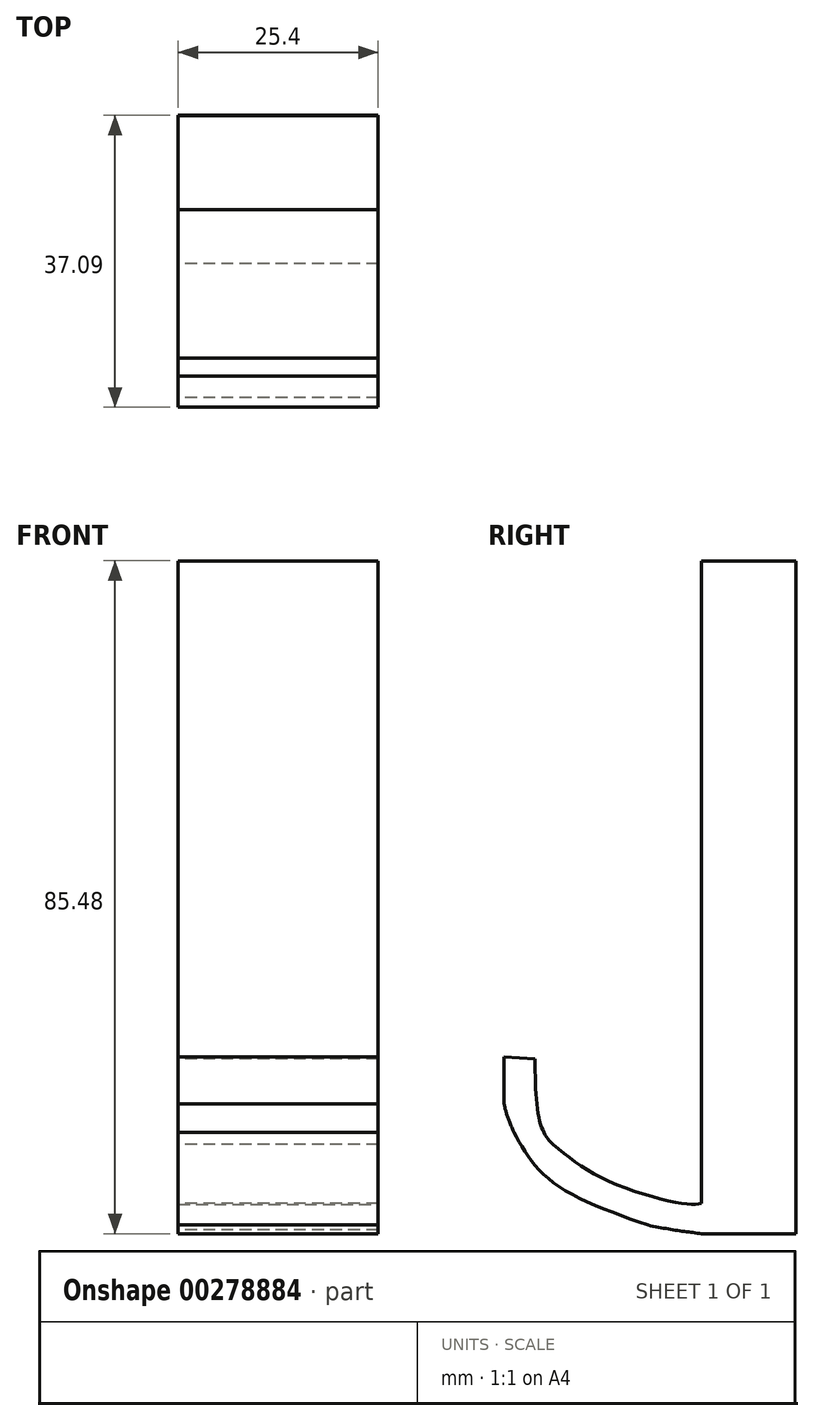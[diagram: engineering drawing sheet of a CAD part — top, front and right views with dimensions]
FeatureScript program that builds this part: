
annotation { "Feature Type Name" : "Feature", "Feature Type Description" : "" }
export const myFeature = defineFeature(function(context is Context, id is Id, definition is map)
    precondition{}
    {
        {
            var Q0;
            Q0=qCreatedBy(makeId("Right.planeOp"),FACE);
            var sketch = newSketch(context, id + "F0", { "sketchPlane" : qUnion([Q0])});
            skLineSegment(sketch, "E0", {"start": v(0, 56.23) * mm, "end": v(0, 0) * mm});
            skLineSegment(sketch, "E1", {"start": v(0, 0) * mm, "end": v(0, -25.43) * mm});
            skLineSegment(sketch, "E2", {"start": v(0, 56.23) * mm, "end": v(11.98, 56.23) * mm});
            skLineSegment(sketch, "E3", {"start": v(11.98, 56.23) * mm, "end": v(11.98, -28.76) * mm});
            skLineSegment(sketch, "E4", {"start": v(0, -29.25) * mm, "end": v(12, -29.25) * mm});
            skLineSegment(sketch, "E5", {"start": v(12, -29.25) * mm, "end": v(11.98, -28.76) * mm});
            skFitSpline(sketch, "E6", {"points": [v(-18.86, -17.93) * mm, v(-12.1, -22.45) * mm, v(-2.16, -25.45) * mm, v(0, -25.43) * mm], "startDerivative": vector(15.44, -12.93) * mm, "endDerivative": vector(8.77, 1.1) * mm});
            skLineSegment(sketch, "E7", {"start": v(-25.1, -10.73) * mm, "end": v(-25.1, -6.83) * mm});
            skLineSegment(sketch, "E8", {"start": v(-25.1, -6.83) * mm, "end": v(-21.14, -7.06) * mm});
            skFitSpline(sketch, "E9", {"points": [v(-20.78, 0.17) * mm, v(-20.78, -13.9) * mm, v(-18.86, -17.93) * mm], "startDerivative": vector(-0.98, -6.3) * mm, "endDerivative": vector(6.33, -5.9) * mm});
            skFitSpline(sketch, "E10", {"points": [v(-25.1, -10.73) * mm, v(-25.1, -12.78) * mm], "startDerivative": vector(0, -2.05) * mm, "endDerivative": vector(0, -2.05) * mm});
            skFitSpline(sketch, "E11", {"points": [v(-25.1, -12.78) * mm, v(-24.62, -14.46) * mm, v(-22.88, -18.4) * mm, v(-18.96, -23.6) * mm, v(-7.34, -28.05) * mm, v(0, -29.25) * mm], "startDerivative": vector(3.29, -14.1) * mm, "endDerivative": vector(29.67, -3.67) * mm});
            skFitSpline(sketch, "E12", {"points": [v(-23.84, -16.35) * mm, v(-21.6, -20.03) * mm, v(-17.1, -23.9) * mm, v(-6.83, -28.16) * mm], "startDerivative": vector(7.49, -14.15) * mm, "endDerivative": vector(26.63, -9.4) * mm});
            skSolve(sketch);
        }
        {
            var Q0;
            Q0=makeQuery(id+"F0.imprint","IMPRINT",FACE,{"disambiguationData":[TD([[makeQuery(id+"F0.imprint","IMPRINT",EDGE,{"derivedFrom":sQuery(id+"F0.wireOp",EDGE,"E0")}),1.0]])]});
            extrude(context, id + "F1", {"entities" : qUnion([Q0]), "depth" : 25.4 * mm});
        }
    });
